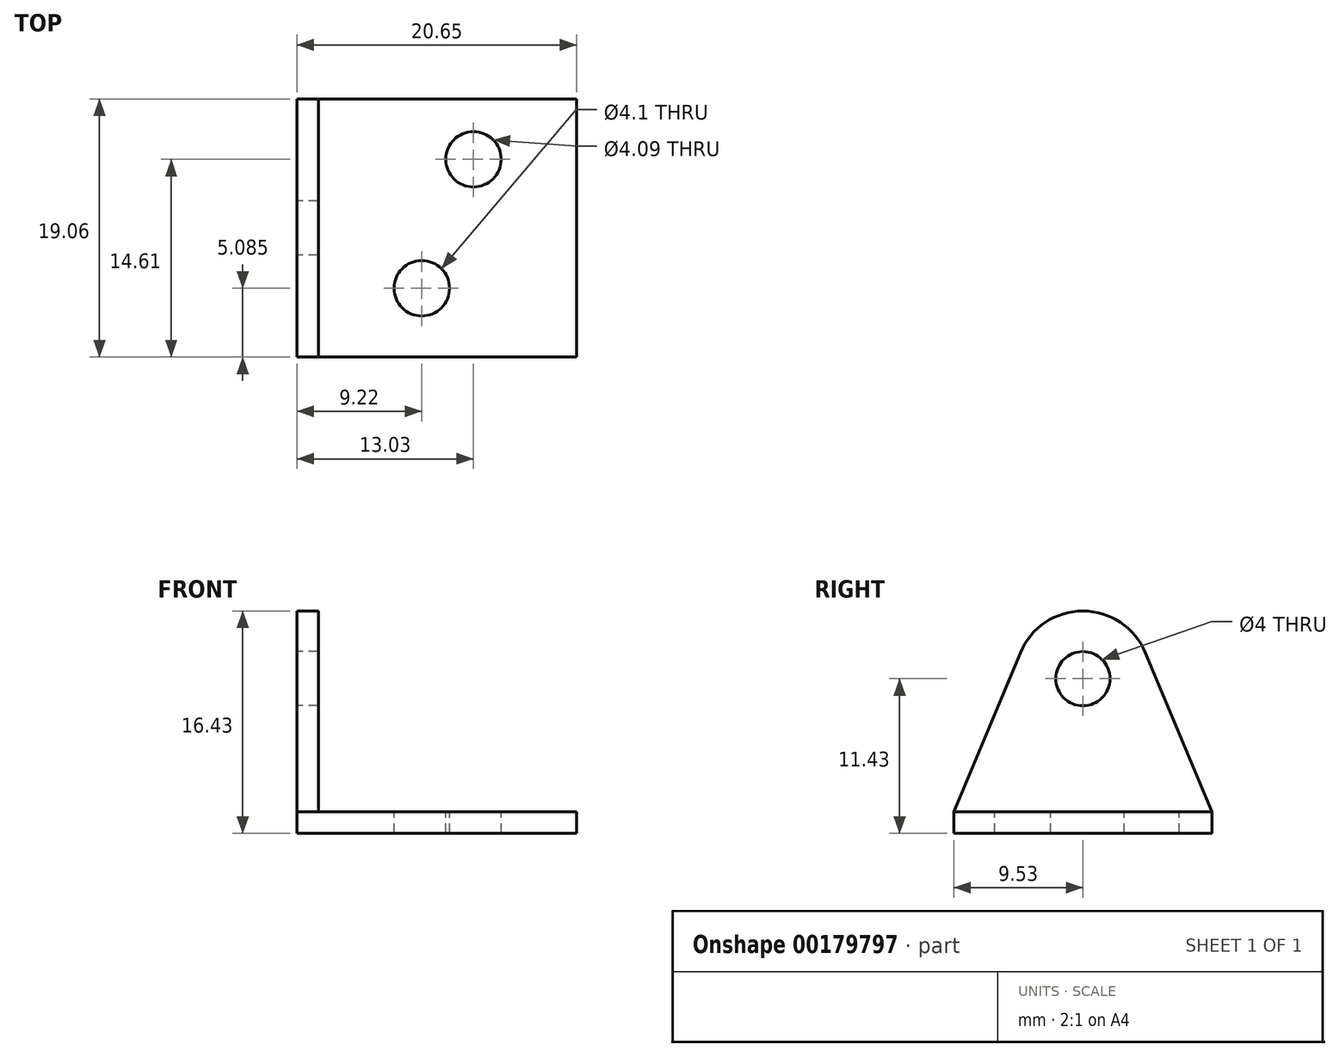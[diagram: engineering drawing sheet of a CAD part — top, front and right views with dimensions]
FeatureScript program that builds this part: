
annotation { "Feature Type Name" : "Feature", "Feature Type Description" : "" }
export const myFeature = defineFeature(function(context is Context, id is Id, definition is map)
    precondition{}
    {
        {
            var Q0;
            Q0=qCreatedBy(makeId("Front.planeOp"),FACE);
            var sketch = newSketch(context, id + "F0", { "sketchPlane" : qUnion([Q0])});
            skLineSegment(sketch, "E0", {"start": v(0, 19.05) * mm, "end": v(0, 0) * mm});
            skLineSegment(sketch, "E1", {"start": v(0, 0) * mm, "end": v(20.65, 0) * mm});
            skLineSegment(sketch, "E2", {"start": v(20.65, 0) * mm, "end": v(20.65, 1.6) * mm});
            skLineSegment(sketch, "E3", {"start": v(20.65, 1.6) * mm, "end": v(1.6, 1.6) * mm});
            skLineSegment(sketch, "E4", {"start": v(1.6, 1.6) * mm, "end": v(1.6, 19.05) * mm});
            skLineSegment(sketch, "E5", {"start": v(1.6, 19.05) * mm, "end": v(0, 19.05) * mm});
            skPoint(sketch, "E6.visualSharp", {"position": v(1.6, 1.6) * mm});
            skSolve(sketch);
        }
        {
            var Q0;
            Q0=qSketchRegion(id+"F0",true);
            extrude(context, id + "F1", {"entities" : qUnion([Q0]), "endBound" : BoundingType.SYMMETRIC, "depth" : 19.05 * mm});
        }
        {
            var Q0;
            Q0=makeQuery(id+"F1.opExtrude","SWEPT_FACE",FACE,{"disambiguationData":[OSD([sQuery(id+"F0.wireOp",EDGE,"E0")])]});
            var sketch = newSketch(context, id + "F2", { "sketchPlane" : qUnion([Q0])});
            skCircle(sketch, "E7", {"center": v(0, 11.43) * mm, "radius": 2 * mm});
            skSolve(sketch);
        }
        {
            var Q0;
            Q0=qSketchRegion(id+"F2",true);
            extrude(context, id + "F3", {"entities" : qUnion([Q0]), "operationType" : NewBodyOperationType.REMOVE, "endBound" : BoundingType.UP_TO_NEXT, "oppositeDirection" : true, "depth" : 25.4 * mm});
        }
        {
            var Q0;
            Q0=makeQuery(id+"F1.opExtrude","SWEPT_FACE",FACE,{"disambiguationData":[OSD([sQuery(id+"F0.wireOp",EDGE,"E0")])]});
            var sketch = newSketch(context, id + "F4", { "sketchPlane" : qUnion([Q0])});
            skLineSegment(sketch, "E8", {"start": v(-9.53, 0) * mm, "end": v(9.53, 0) * mm});
            skLineSegment(sketch, "E9", {"start": v(-4.61, 13.36) * mm, "end": v(-9.53, 1.6) * mm});
            skLineSegment(sketch, "E10", {"start": v(-9.53, 1.6) * mm, "end": v(-9.53, 0) * mm});
            skArc(sketch, "E11", {"start": v(0, 16.43) * mm, "mid": v(-2.77, 15.6) * mm, "end": v(-4.61, 13.36) * mm});
            skLineSegment(sketch, "E12", {"start": v(0, 11.43) * mm, "end": v(0, 12.8) * mm, "construction": true});
            skArc(sketch, "E13.MirrorCS", {"start": v(0, 16.43) * mm, "mid": v(2.77, 15.6) * mm, "end": v(4.61, 13.36) * mm});
            skLineSegment(sketch, "E14.MirrorCS", {"start": v(9.53, 1.6) * mm, "end": v(9.53, 0) * mm});
            skLineSegment(sketch, "E15.MirrorCS", {"start": v(4.61, 13.36) * mm, "end": v(9.53, 1.6) * mm});
            skSolve(sketch);
        }
        {
            var Q0;
            Q0=makeQuery(id+"F4.imprint","IMPRINT",FACE,{"disambiguationData":[TD([[makeQuery(id+"F4.imprint","IMPRINT",EDGE,{"derivedFrom":sQuery(id+"F4.wireOp",EDGE,"O1OHdn4o-TkjY-Bv5V-2hQo-R17gs5ZTKX2j")}),-1.0]])]});
            var Q1;
            {var subQ1=sQuery(id+"F4.wireOp",EDGE,"E9");Q1=makeQuery(id+"F4.imprint","IMPRINT",FACE,{"disambiguationData":[TD([[makeQuery(id+"F4.imprint","IMPRINT",EDGE,{"derivedFrom":subQ1}),-1.0]])]});}
            extrude(context, id + "F5", {"entities" : qUnion([Q0, Q1]), "operationType" : NewBodyOperationType.REMOVE, "endBound" : BoundingType.UP_TO_NEXT, "oppositeDirection" : true, "depth" : 25.4 * mm});
        }
        {
            var Q0;
            Q0=makeQuery(id+"F1.opExtrude","SWEPT_FACE",FACE,{"disambiguationData":[OSD([sQuery(id+"F0.wireOp",EDGE,"E3")])]});
            var sketch = newSketch(context, id + "F6", { "sketchPlane" : qUnion([Q0])});
            skCircle(sketch, "E16", {"center": v(13.03, 5.08) * mm, "radius": 2.04 * mm});
            skCircle(sketch, "E17.MirrorC", {"center": v(9.22, -4.44) * mm, "radius": 2.05 * mm});
            skSolve(sketch);
        }
        {
            var Q0;
            Q0 = qSketchRegion(id + "F6", true);
            extrude(context, id + "F7", {"entities" : qUnion([Q0]), "operationType" : NewBodyOperationType.REMOVE, "endBound" : BoundingType.UP_TO_NEXT, "oppositeDirection" : true, "depth" : 25.4 * mm});
        }
    });
